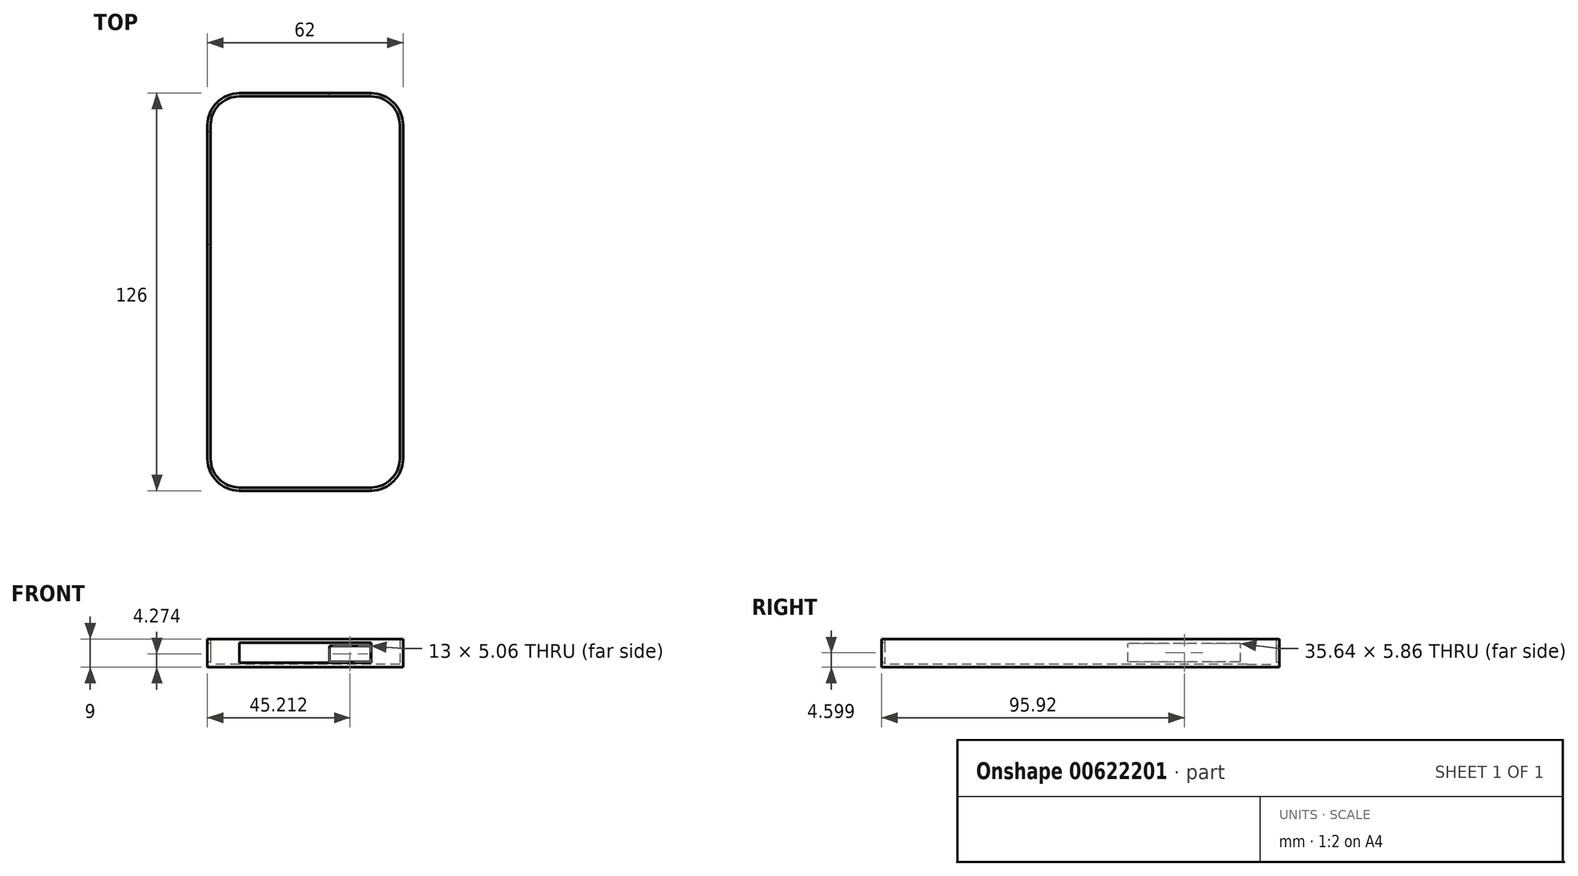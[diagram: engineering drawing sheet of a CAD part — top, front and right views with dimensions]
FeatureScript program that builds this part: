
annotation { "Feature Type Name" : "Feature", "Feature Type Description" : "" }
export const myFeature = defineFeature(function(context is Context, id is Id, definition is map)
    precondition{}
    {
        {
            var Q0;
            Q0=qCreatedBy(makeId("Top.planeOp"),FACE);
            var sketch = newSketch(context, id + "F0", { "sketchPlane" : qUnion([Q0])});
            skLineSegment(sketch, "E0.bottom", {"start": v(20.84, 63) * mm, "end": v(-20.84, 63) * mm});
            skLineSegment(sketch, "E0.top", {"start": v(20.84, -63) * mm, "end": v(-20.84, -63) * mm});
            skLineSegment(sketch, "E0.left", {"start": v(31, 52.84) * mm, "end": v(31, -52.84) * mm});
            skLineSegment(sketch, "E0.right", {"start": v(-31, 52.84) * mm, "end": v(-31, -52.84) * mm});
            skPoint(sketch, "E0.middle", {"position": v(0, 0) * mm});
            skPoint(sketch, "E1.visualSharp", {"position": v(-31, 63) * mm});
            skArc(sketch, "E1.filletArc", {"start": v(-20.84, 63) * mm, "mid": v(-28.02, 60.02) * mm, "end": v(-31, 52.84) * mm});
            skPoint(sketch, "E2.visualSharp", {"position": v(31, 63) * mm});
            skArc(sketch, "E2.filletArc", {"start": v(31, 52.84) * mm, "mid": v(28.02, 60.02) * mm, "end": v(20.84, 63) * mm});
            skPoint(sketch, "E3.visualSharp", {"position": v(31, -63) * mm});
            skArc(sketch, "E3.filletArc", {"start": v(20.84, -63) * mm, "mid": v(28.02, -60.02) * mm, "end": v(31, -52.84) * mm});
            skPoint(sketch, "E4.visualSharp", {"position": v(-31, -63) * mm});
            skArc(sketch, "E4.filletArc", {"start": v(-31, -52.84) * mm, "mid": v(-28.02, -60.02) * mm, "end": v(-20.84, -63) * mm});
            skSolve(sketch);
        }
        {
            var Q0;
            Q0 = qSketchRegion(id + "F0", true);
            extrude(context, id + "F1", {"entities" : qUnion([Q0]), "depth" : 9 * mm, "offsetDistance" : 25 * mm});
        }
        {
            var Q0;
            Q0=makeQuery(id+"F1.opExtrude","CAP_FACE",FACE,{"disambiguationData":[OSD([sQuery(id+"F0.wireOp",EDGE,"E0.bottom"),sQuery(id+"F0.wireOp",EDGE,"E0.top"),sQuery(id+"F0.wireOp",EDGE,"E0.left"),sQuery(id+"F0.wireOp",EDGE,"E0.right")])],"isStart":false});
            shell(context, id + "F2", {"entities" : qUnion([Q0]), "thickness" : 1 * mm});
        }
        {
            var Q0;
            Q0=makeQuery(id+"F1.opExtrude","SWEPT_FACE",FACE,{"disambiguationData":[OSD([sQuery(id+"F0.wireOp",EDGE,"E0.bottom")])]});
            var sketch = newSketch(context, id + "F3", { "sketchPlane" : qUnion([Q0])});
            skLineSegment(sketch, "E5.bottom", {"start": v(-20.71, 1.74) * mm, "end": v(-7.71, 1.74) * mm});
            skLineSegment(sketch, "E5.top", {"start": v(-20.71, 6.8) * mm, "end": v(-7.71, 6.8) * mm});
            skLineSegment(sketch, "E5.left", {"start": v(-20.71, 1.74) * mm, "end": v(-20.71, 6.8) * mm});
            skLineSegment(sketch, "E5.right", {"start": v(-7.71, 1.74) * mm, "end": v(-7.71, 6.8) * mm});
            skPoint(sketch, "E5.middle", {"position": v(-14.21, 4.27) * mm});
            skSolve(sketch);
        }
        {
            var Q0;
            Q0 = qSketchRegion(id + "F3", true);
            extrude(context, id + "F4", {"entities" : qUnion([Q0]), "operationType" : NewBodyOperationType.REMOVE, "oppositeDirection" : true, "depth" : 8.9 * mm, "offsetDistance" : 25 * mm});
        }
        {
            var Q0;
            Q0=makeQuery(id+"F1.opExtrude","SWEPT_FACE",FACE,{"disambiguationData":[OSD([sQuery(id+"F0.wireOp",EDGE,"E0.right")])]});
            var sketch = newSketch(context, id + "F5", { "sketchPlane" : qUnion([Q0])});
            skLineSegment(sketch, "E6.bottom", {"start": v(-50.74, 1.67) * mm, "end": v(-15.1, 1.67) * mm});
            skLineSegment(sketch, "E6.top", {"start": v(-50.74, 7.53) * mm, "end": v(-15.1, 7.53) * mm});
            skLineSegment(sketch, "E6.left", {"start": v(-50.74, 1.67) * mm, "end": v(-50.74, 7.53) * mm});
            skLineSegment(sketch, "E6.right", {"start": v(-15.1, 1.67) * mm, "end": v(-15.1, 7.53) * mm});
            skSolve(sketch);
        }
        {
            var Q0;
            Q0=makeQuery(id+"F5.imprint","IMPRINT",FACE,{"disambiguationData":[TD([[makeQuery(id+"F5.imprint","IMPRINT",EDGE,{"derivedFrom":sQuery(id+"F5.wireOp",EDGE,"E6.bottom")}),1.0]])]});
            extrude(context, id + "F6", {"entities" : qUnion([Q0]), "operationType" : NewBodyOperationType.REMOVE, "oppositeDirection" : true, "depth" : 9.9 * mm, "offsetDistance" : 25 * mm});
        }
        {
            var Q0;
            Q0=makeQuery(id+"F1.opExtrude","SWEPT_FACE",FACE,{"disambiguationData":[OSD([sQuery(id+"F0.wireOp",EDGE,"E0.top")])]});
            var sketch = newSketch(context, id + "F7", { "sketchPlane" : qUnion([Q0])});
            skLineSegment(sketch, "E7.bottom", {"start": v(-20.84, 1.4) * mm, "end": v(20.84, 1.4) * mm});
            skLineSegment(sketch, "E7.top", {"start": v(-20.84, 7.82) * mm, "end": v(20.84, 7.82) * mm});
            skLineSegment(sketch, "E7.left", {"start": v(-20.84, 1.4) * mm, "end": v(-20.84, 7.82) * mm});
            skLineSegment(sketch, "E7.right", {"start": v(20.84, 1.4) * mm, "end": v(20.84, 7.82) * mm});
            skPoint(sketch, "E7.middle", {"position": v(0, 4.6) * mm});
            skSolve(sketch);
        }
        {
            var Q0;
            Q0=makeQuery(id+"F7.imprint","IMPRINT",FACE,{"disambiguationData":[TD([[makeQuery(id+"F7.imprint","IMPRINT",EDGE,{"derivedFrom":sQuery(id+"F7.wireOp",EDGE,"E7.bottom")}),1.0]])]});
            extrude(context, id + "F8", {"entities" : qUnion([Q0]), "operationType" : NewBodyOperationType.REMOVE, "oppositeDirection" : true, "depth" : 25 * mm, "offsetDistance" : 25 * mm});
        }
    });
